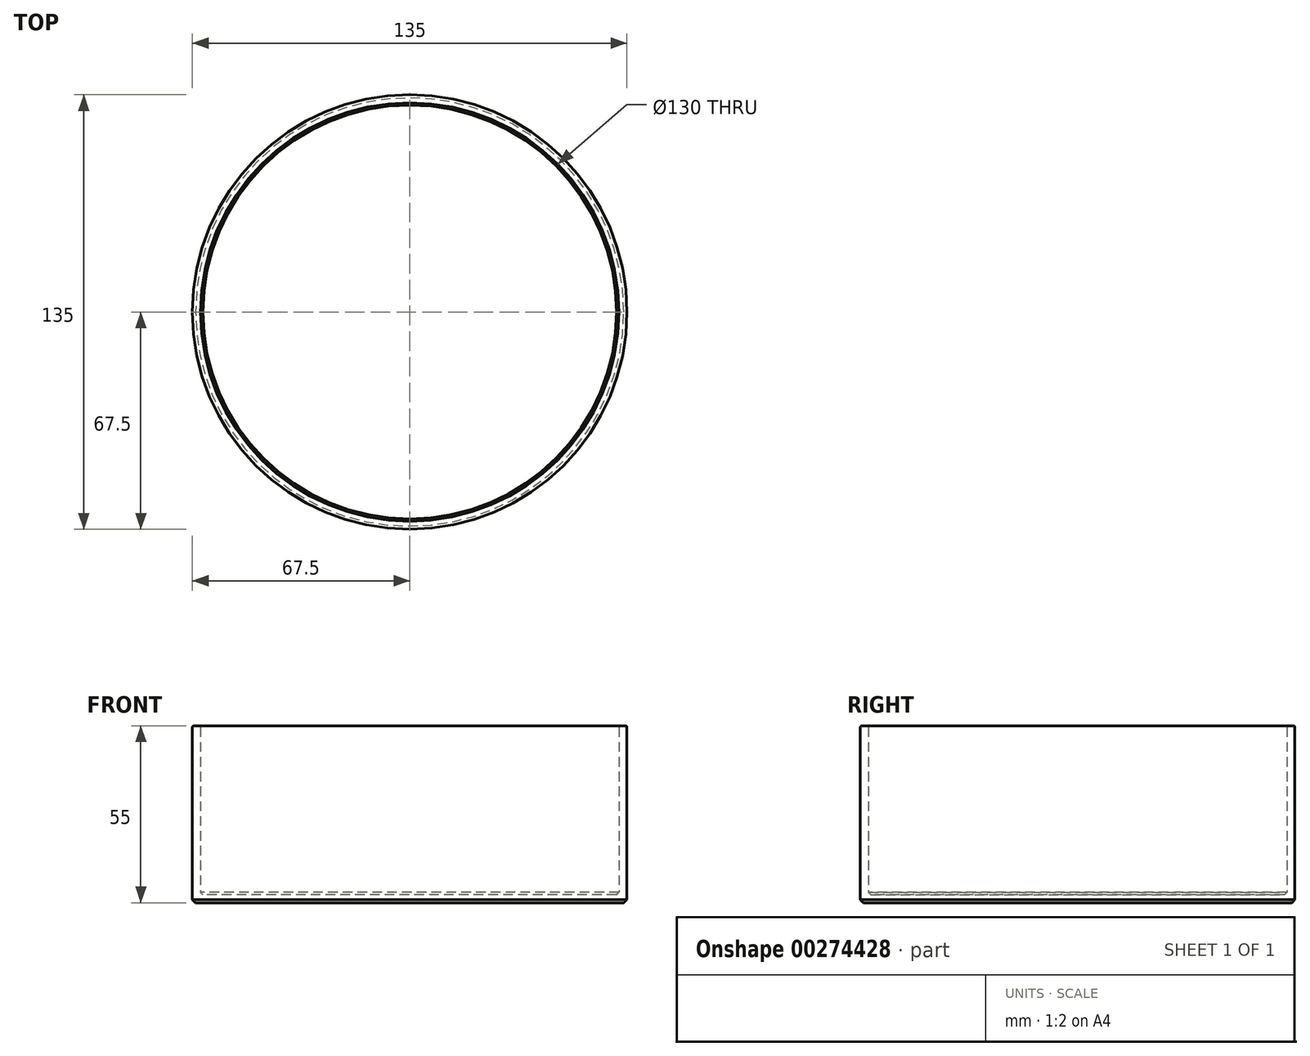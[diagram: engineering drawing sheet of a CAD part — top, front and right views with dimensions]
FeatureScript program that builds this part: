
annotation { "Feature Type Name" : "Feature", "Feature Type Description" : "" }
export const myFeature = defineFeature(function(context is Context, id is Id, definition is map)
    precondition{}
    {
        {
            var Q0;
            Q0=qCreatedBy(makeId("Top.planeOp"),FACE);
            var sketch = newSketch(context, id + "F0", { "sketchPlane" : qUnion([Q0])});
            skCircle(sketch, "E0", {"center": v(0, 0) * mm, "radius": 67.5 * mm});
            skSolve(sketch);
        }
        {
            var Q0;
            Q0=makeQuery(id+"F0.imprint","IMPRINT",FACE,{"disambiguationData":[TD([[makeQuery(id+"F0.imprint","IMPRINT",EDGE,{"derivedFrom":sQuery(id+"F0.wireOp",EDGE,"E0")}),1.0]])]});
            extrude(context, id + "F1", {"entities" : qUnion([Q0]), "depth" : 55 * mm});
        }
        {
            var Q0;
            Q0=makeQuery(id+"F1.opExtrude","CAP_FACE",FACE,{"disambiguationData":[OSD([sQuery(id+"F0.wireOp",EDGE,"E0")])],"isStart":false});
            shell(context, id + "F2", {"entities" : qUnion([Q0]), "thickness" : 2.5 * mm});
        }
        {
            var Q0;
            Q0=makeQuery(id+"F1.opExtrude","CAP_EDGE",EDGE,{"disambiguationData":[OSD([sQuery(id+"F0.wireOp",EDGE,"E0")])],"isStart":false});
            var Q1;
            {var subQ0=sQuery(id+"F0.wireOp",EDGE,"E0");Q1=makeQuery(id+"F2.opShell","OFFSET_EDGE",EDGE,{"disambiguationData":[OSD([subQ0]),TDD([makeQuery(id+"F1.opExtrude","CAP_EDGE",EDGE,{"disambiguationData":[OSD([subQ0])],"isStart":false})])]});}
            fillet(context, id + "F3", {"entities" : qUnion([Q0, Q1]), "radius" : .5 * mm, "tangentPropagation" : true, "allowEdgeOverflow" : false});
        }
        {
            var Q0;
            Q0=makeQuery(id+"F1.opExtrude","CAP_EDGE",EDGE,{"disambiguationData":[OSD([sQuery(id+"F0.wireOp",EDGE,"E0")])],"isStart":true});
            chamfer(context, id + "F4", {"entities" : qUnion([Q0]), "width" : 1 * mm, "tangentPropagation" : true});
        }
        {
            var Q0;
            {var subQ0=sQuery(id+"F0.wireOp",EDGE,"E0");Q0=makeQuery(id+"F2.opShell","OFFSET_EDGE",EDGE,{"disambiguationData":[OSD([subQ0]),TDD([makeQuery(id+"F1.opExtrude","CAP_EDGE",EDGE,{"disambiguationData":[OSD([subQ0])],"isStart":true})])]});}
            chamfer(context, id + "F5", {"entities" : qUnion([Q0]), "width" : .75 * mm, "tangentPropagation" : true});
        }
    });
